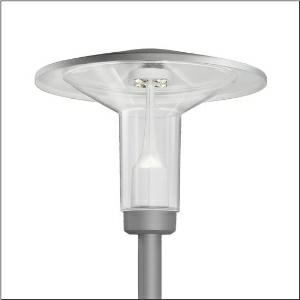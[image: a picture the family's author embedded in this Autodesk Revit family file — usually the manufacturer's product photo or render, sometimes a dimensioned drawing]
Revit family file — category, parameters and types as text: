
# Revit family: laterne_iq___st1_2a_5xa5255mf14h_e85f
name_source: partatom
category: Lighting Fixtures
units: mm (PartAtom-declared; Revit-internal decimal feet)

## family parameters
Cut with Voids When Loaded = No
Host = Face
Light Source = No
Part Type = Normal
Room Calculation Point = No
Round Connector Dimension = Use Diameter
Shared = No

## types (1)
- --- (1 x LED, 1540 lm, 11.8 W, 2700K)
    Apparent Load = 12 VA
    CIE Flux Codes = 25 63 94 98 100
    Color Rendering = 70
    Color Temperature = 2700K
    Default Elevation = 1800 mm
    Description = Lantern iQ, mast luminaire, Module 540 iQ-SR, primary light control with 3 zone facetted reflector, of plastic, silver coated, highly specular, structured, primary optical cover: cover, of PMMA, transparent, light distribution: ST1.2a, light emission: direct distribution, primary light characteristic: asymmetric, installation type: post-top, LED, High Power LED, rated luminous flux: 1.540lm, luminous efficacy: 131lm/W, light colour: 727, colour temperature: 2700K, control gear: ECG iQ, control: presetting dimming logarithmic, Street-Remote, Auto-Match, Temp-Guard, Lumen-Switch, Night-Set, Smart-Wire, Light-Fading, Desk-Remote (wireless, voltage-free reading and setting of iQ features in the workshop via application-optimized NFC function/RFID function), optimised constant luminous flux control (CLO 2.0), with terminal, 6-pole, max. 2.5mm², mains connection: 220..240V, AC, 50/60Hz, start of lifetime: 12W, end of lifetime: 12W, reduction: 6W, luminaire housing, upper part, of glass-fibre reinforced polyester, coated, Siteco® metallic grey (DB 702S), diameter: 750mm, height: 583mm, spigot size: d x l = 76 x 70mm (post-top) | with reducer (optional accessory) 60 x 70mm, post-top mast mounting element, of diecast aluminium, coated, Siteco® metallic grey (DB 702S), Module 540 iQ-SR, traffic white (RAL 9016), equipment: standard, protection rating (complete): IP65, insulation class (complete): insulation class II (safety insulation), certification: CE, ENEC, VDE, packaging unit: 1 piece

Light Distribution: ST1.2a
    Height = 583 mm
    Lamp = 1 x LED
    Lamp Light Flux = 1540 lm
    Lamp Power = 11.8 W
    Lamp count = 1
    Length = 750 mm
    Luminous efficacy = 131 lm/W
    Manufacturer = Siteco
    ModVariant = No
    Model = 5XA5255MF14H
    Number of Poles = 1
    OnlyDefault = Yes
    Power Factor = 1
    Product Name = Laterne iQ | ST1.2a
    Product group = mast luminaire | pylon top
    ProductGroupID = 6100
    Protection Class = Protection class II
    Protection Degree = IP 65
    RLX_Detail_Level = 1
    RlxData = <blob elided: 103445 chars, md5=914d2bc3>
    Socket = socket
    Standby Power = 0 W
    System Light Flux = 1540 lm
    System Power = 12 W
    Type Comments = factory setting: luminous flux: 100 % | dim-lin: 254 | 472 mA
    Type Image = l_1006050.jpg
    URL = http://relux.com
    VarID = @adj_063249
    Voltage = 0 V
    Weight = 0.00 kg
    Width = 0 mm  [stored 0 ft]

note: [stored X ft] marks values corroborated as IEEE doubles in the binary element streams (Revit-internal decimal feet)

## geometry (parser evidence)
native form markers: Blend x4, Sweep x10
no freeform markers — native parametric forms only
